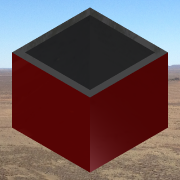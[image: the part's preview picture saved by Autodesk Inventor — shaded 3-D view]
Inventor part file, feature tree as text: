
AUTODESK INVENTOR PART (.ipt)
format: ipt  version: 2014 SP1 (Build 180222100, 222)  size: 114,176 bytes
history: native  units: in
note: dims shown in document units (in); Inventor stores cm internally (conversion verified against a paired STEP export)
features: extrude x1, sketch x1
ambient origin geometry x8: Origin, YZ Plane, XZ Plane, XY Plane, X Axis, Y Axis, Z Axis, Center Point
bodies: Solid1 (feature_tree)
feature tree (2):
  extrude  "Extrusion1"  Depth=1.0in
  sketch  "Sketch1"  dims[d0=1.0in d1=1.0in d2=0.1in d3=1.0in d4=0.0in]
